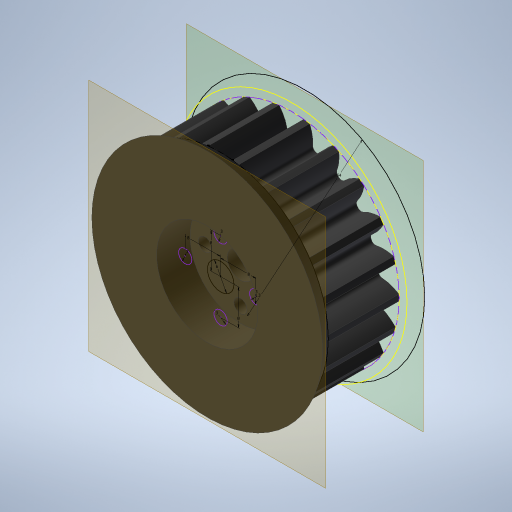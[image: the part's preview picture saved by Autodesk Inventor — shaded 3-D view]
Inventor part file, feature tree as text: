
AUTODESK INVENTOR PART (.ipt)
format: ipt  version: 2024.2 (Build 282272000, 272)  size: 508,416 bytes
history: native  units: mm
features: sketch x6, extrude x5, other x3, pattern_circular x1, loft x1, projected_geometry x1
ambient origin geometry x8: Origin, YZ Plane, XZ Plane, XY Plane, X Axis, Y Axis, Z Axis, Center Point
bodies: Body1 (feature_tree)
feature tree (17):
  other  "Твердое тело1"
  sketch  "Sketch1"  dims[d0=16.0mm d1=0.0mm d4=0.0mm d5=0.0mm d6=220.0mm d7=360.0deg d9=6.0mm d10=3.0mm d11=3.0mm d12=3.0mm d13=3.0mm d14=8.0mm d15=8.0mm d16=8.0mm d17=8.0mm d18=3.0mm d19=10.0mm d20=0.0mm d21=0.0mm d22=3.0mm d23=52.0mm d24=0.0mm d25=90.0deg d26=0.0mm d27=90.0deg d28=22.8mm d29=7.5mm d30=0.0mm d31=3.0mm d32=0.0mm d33=3.0mm d38=54.0mm]
  extrude  "Выдавливание1"  TaperAngle=0.0deg  [1 undecoded]
  extrude  "Выдавливание2"  TaperAngle=0.0deg  [1 undecoded]
  pattern_circular  "Круговой массив1"  Count=22 Angle=360.0deg
  extrude  "Выдавливание3"  Depth=10.0mm
  other  "РабПлоскость1"
  loft  "Лофт1"
  extrude  "Выдавливание4"  Depth=10.0mm
  extrude  "Выдавливание5"  Depth=10.0mm
  sketch  "Эскиз5"
  other  "РабПлоскость2"
  sketch  "Эскиз6"
  sketch  "Эскиз2"
  sketch  "Эскиз3"
  sketch  "Эскиз4"
  projected_geometry  "Спроецированная петля1"
note: 2 required parameter values undecoded (feature->parameter linkage not recoverable at this tier; creation-order binding heuristic only, values carry confidence <= 0.55)
